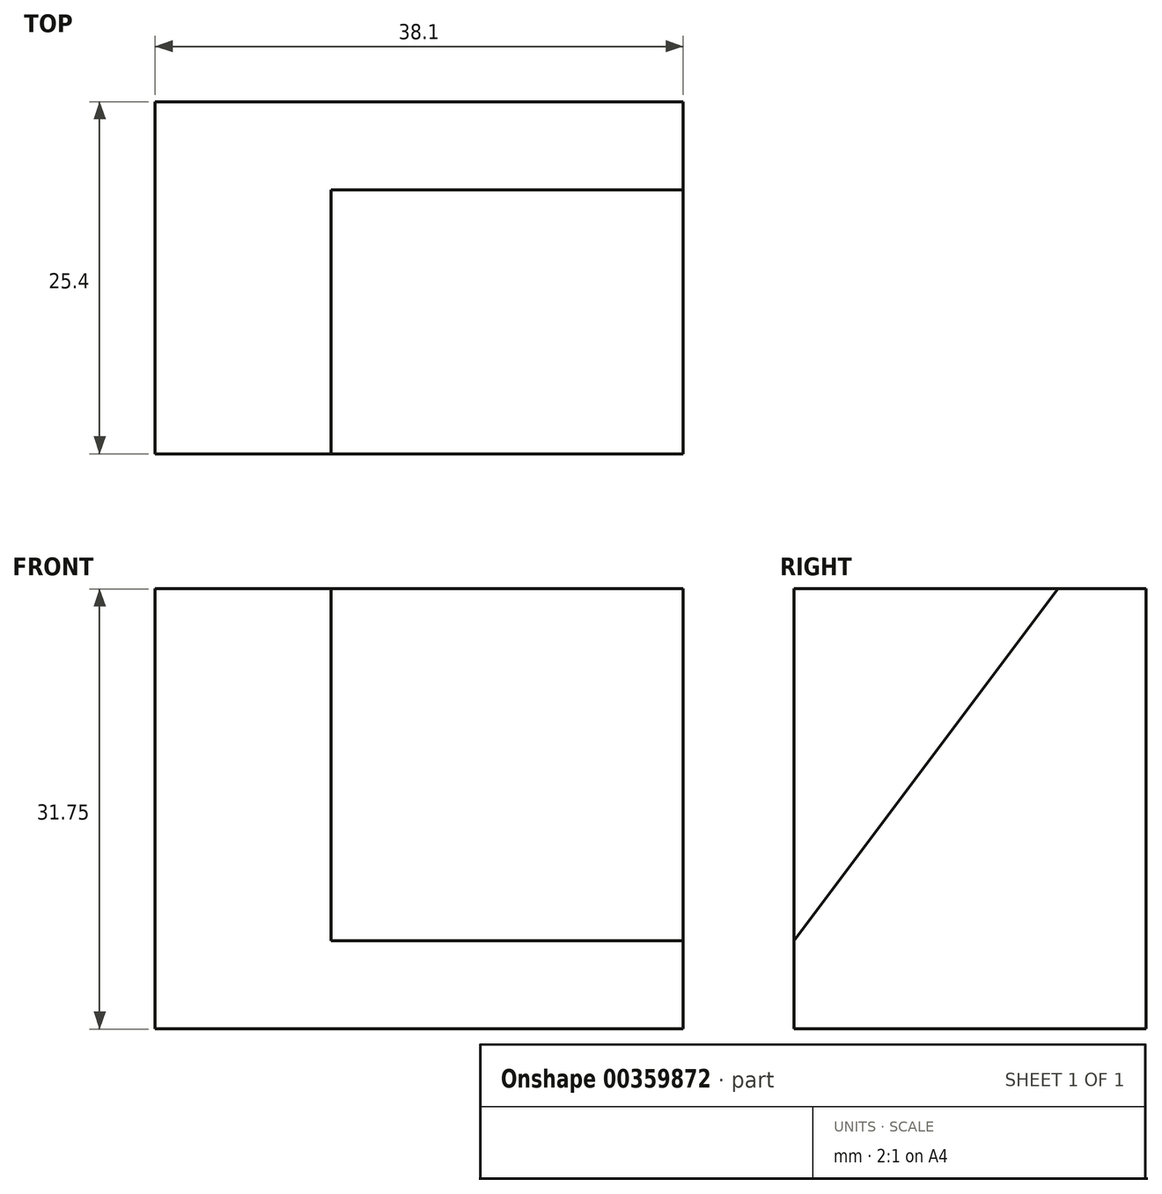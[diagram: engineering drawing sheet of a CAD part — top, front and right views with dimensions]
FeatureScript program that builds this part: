
annotation { "Feature Type Name" : "Feature", "Feature Type Description" : "" }
export const myFeature = defineFeature(function(context is Context, id is Id, definition is map)
    precondition{}
    {
        {
            var Q0;
            Q0=qCreatedBy(makeId("Front.planeOp"),FACE);
            var sketch = newSketch(context, id + "F0", { "sketchPlane" : qUnion([Q0])});
            skLineSegment(sketch, "E0", {"start": v(-18.84, -13.92) * mm, "end": v(-18.84, -45.67) * mm});
            skLineSegment(sketch, "E1", {"start": v(-18.84, -45.67) * mm, "end": v(19.26, -45.67) * mm});
            skLineSegment(sketch, "E2", {"start": v(19.26, -45.67) * mm, "end": v(19.26, -13.92) * mm});
            skLineSegment(sketch, "E3", {"start": v(-18.84, -13.92) * mm, "end": v(19.26, -13.92) * mm});
            skSolve(sketch);
        }
        {
            var Q0;
            Q0 = qSketchRegion(id + "F0", true);
            extrude(context, id + "F1", {"entities" : qUnion([Q0]), "depth" : 25.4 * mm});
        }
        {
            var Q0;
            Q0=makeQuery(id+"F1.opExtrude","SWEPT_FACE",FACE,{"disambiguationData":[OSD([sQuery(id+"F0.wireOp",EDGE,"E2")])]});
            var sketch = newSketch(context, id + "F2", { "sketchPlane" : qUnion([Q0])});
            skLineSegment(sketch, "E4", {"start": v(-25.4, -13.92) * mm, "end": v(-25.4, -39.32) * mm});
            skLineSegment(sketch, "E5", {"start": v(-25.4, -39.32) * mm, "end": v(-6.35, -13.92) * mm});
            skLineSegment(sketch, "E6", {"start": v(-6.35, -13.92) * mm, "end": v(-25.4, -13.92) * mm});
            skSolve(sketch);
        }
        {
            var Q0;
            Q0 = qSketchRegion(id + "F2", true);
            extrude(context, id + "F3", {"entities" : qUnion([Q0]), "operationType" : NewBodyOperationType.REMOVE, "oppositeDirection" : true, "depth" : 25.4 * mm});
        }
    });
